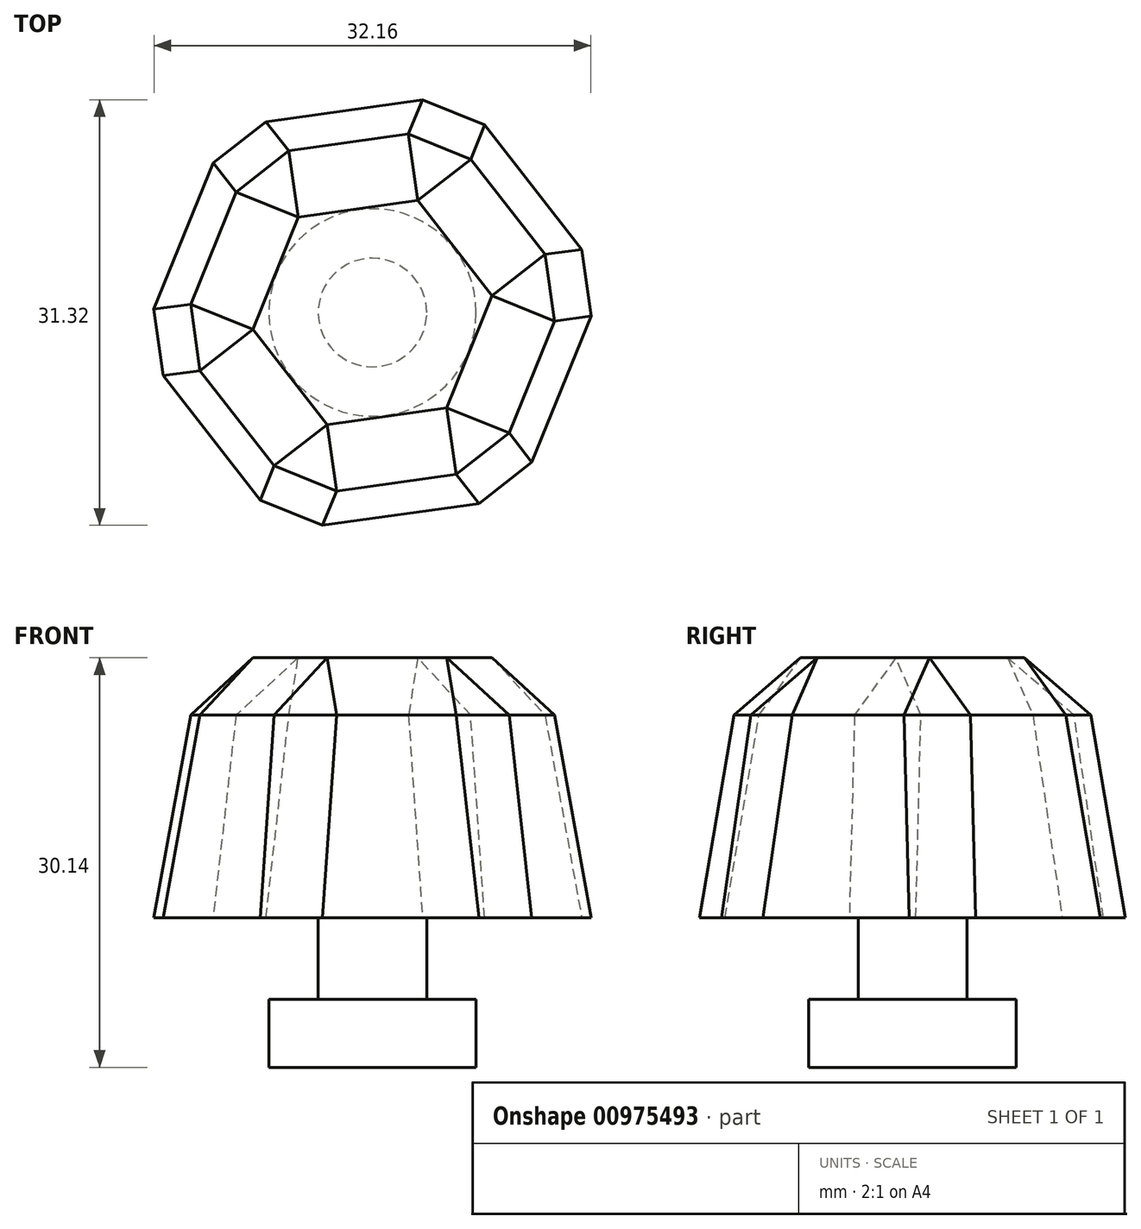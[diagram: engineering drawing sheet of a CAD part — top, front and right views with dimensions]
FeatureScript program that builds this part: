
annotation { "Feature Type Name" : "Feature", "Feature Type Description" : "" }
export const myFeature = defineFeature(function(context is Context, id is Id, definition is map)
    precondition{}
    {
        {
            var Q0;
            Q0=qCreatedBy(makeId("Top.planeOp"),FACE);
            var sketch = newSketch(context, id + "F0", { "sketchPlane" : qUnion([Q0])});
            skCircle(sketch, "E0.cCircle", {"center": v(0, 0) * mm, "radius": 15 * mm, "construction": true});
            skLineSegment(sketch, "E0.0", {"start": v(17.15, 2.4) * mm, "end": v(10.66, -13.65) * mm});
            skLineSegment(sketch, "E0.1", {"start": v(10.66, -13.65) * mm, "end": v(-6.5, -16.06) * mm});
            skLineSegment(sketch, "E0.2", {"start": v(-6.5, -16.06) * mm, "end": v(-17.15, -2.4) * mm});
            skLineSegment(sketch, "E0.3", {"start": v(-17.15, -2.4) * mm, "end": v(-10.66, 13.65) * mm});
            skLineSegment(sketch, "E0.4", {"start": v(-10.66, 13.65) * mm, "end": v(6.5, 16.06) * mm});
            skLineSegment(sketch, "E0.5", {"start": v(6.5, 16.06) * mm, "end": v(17.15, 2.4) * mm});
            skPoint(sketch, "E0.0.midPoint", {"position": v(13.9, -5.63) * mm});
            skSolve(sketch);
        }
        {
            var Q0;
            Q0=makeQuery(id+"F0.imprint","IMPRINT",FACE,{"disambiguationData":[TD([[makeQuery(id+"F0.imprint","IMPRINT",EDGE,{"derivedFrom":sQuery(id+"F0.wireOp",EDGE,"E0.0")}),-1.0]])]});
            extrude(context, id + "F1", {"entities" : qUnion([Q0]), "depth" : 19.14 * mm, "offsetDistance" : 25 * mm, "hasDraft" : true, "draftAngle" : 9 * degree, "draftPullDirection" : true});
        }
        {
            var Q0;
            Q0=makeQuery(id+"F1.opExtrude","CAP_FACE",FACE,{"disambiguationData":[OSD([sQuery(id+"F0.wireOp",EDGE,"E0.0"),sQuery(id+"F0.wireOp",EDGE,"E0.1"),sQuery(id+"F0.wireOp",EDGE,"E0.2"),sQuery(id+"F0.wireOp",EDGE,"E0.3"),sQuery(id+"F0.wireOp",EDGE,"E0.4"),sQuery(id+"F0.wireOp",EDGE,"E0.5")])],"isStart":true});
            var sketch = newSketch(context, id + "F2", { "sketchPlane" : qUnion([Q0])});
            skCircle(sketch, "E1", {"center": v(0, 0) * mm, "radius": 4 * mm});
            skSolve(sketch);
        }
        {
            var Q0;
            Q0=makeQuery(id+"F2.imprint","IMPRINT",FACE,{"disambiguationData":[TD([[makeQuery(id+"F2.imprint","IMPRINT",EDGE,{"derivedFrom":sQuery(id+"F2.wireOp",EDGE,"E1")}),1.0]])]});
            extrude(context, id + "F3", {"entities" : qUnion([Q0]), "depth" : 6 * mm, "offsetDistance" : 25 * mm});
        }
        {
            var Q0;
            Q0=makeQuery(id+"F3.opExtrude","CAP_FACE",FACE,{"disambiguationData":[OSD([sQuery(id+"F2.wireOp",EDGE,"E1")])],"isStart":false});
            var sketch = newSketch(context, id + "F4", { "sketchPlane" : qUnion([Q0])});
            skCircle(sketch, "E2", {"center": v(0, 0) * mm, "radius": 7.63 * mm});
            skSolve(sketch);
        }
        {
            var Q0;
            Q0=makeQuery(id+"F4.imprint","IMPRINT",FACE,{"disambiguationData":[TD([[makeQuery(id+"F4.imprint","IMPRINT",EDGE,{"derivedFrom":sQuery(id+"F4.wireOp",EDGE,"E2")}),1.0]])]});
            var Q1;
            Q1=makeQuery(id+"F4.imprint","IMPRINT",FACE,{"disambiguationData":[TD([[makeQuery(id+"F4.imprint","IMPRINT",EDGE,{"derivedFrom":makeQuery(id+"F3.opExtrude","CAP_EDGE",EDGE,{"disambiguationData":[OSD([sQuery(id+"F2.wireOp",EDGE,"E1")])],"isStart":false})}),1.0]])]});
            extrude(context, id + "F5", {"entities" : qUnion([Q0, Q1]), "depth" : 5 * mm, "offsetDistance" : 25 * mm});
        }
        {
            var Q0;
            Q0=makeQuery(id+"F1.opExtrude","CAP_EDGE",EDGE,{"disambiguationData":[OSD([sQuery(id+"F0.wireOp",EDGE,"E0.1")])],"isStart":false});
            var Q1;
            Q1=makeQuery(id+"F1.opExtrude","CAP_EDGE",EDGE,{"disambiguationData":[OSD([sQuery(id+"F0.wireOp",EDGE,"E0.2")])],"isStart":false});
            var Q2;
            Q2=makeQuery(id+"F1.opExtrude","CAP_EDGE",EDGE,{"disambiguationData":[OSD([sQuery(id+"F0.wireOp",EDGE,"E0.3")])],"isStart":false});
            var Q3;
            Q3=makeQuery(id+"F1.opExtrude","CAP_FACE",FACE,{"disambiguationData":[OSD([sQuery(id+"F0.wireOp",EDGE,"E0.0"),sQuery(id+"F0.wireOp",EDGE,"E0.1"),sQuery(id+"F0.wireOp",EDGE,"E0.2"),sQuery(id+"F0.wireOp",EDGE,"E0.3"),sQuery(id+"F0.wireOp",EDGE,"E0.4"),sQuery(id+"F0.wireOp",EDGE,"E0.5")])],"isStart":false});
            var Q4;
            Q4=makeQuery(id+"F1.opExtrude","SWEPT_EDGE",EDGE,{"disambiguationData":[OSD([sQuery(id+"F0.wireOp",EDGE,"E0.2"),sQuery(id+"F0.wireOp",EDGE,"E0.3")])]});
            var Q5;
            Q5=makeQuery(id+"F1.opExtrude","SWEPT_EDGE",EDGE,{"disambiguationData":[OSD([sQuery(id+"F0.wireOp",EDGE,"E0.3"),sQuery(id+"F0.wireOp",EDGE,"E0.4")])]});
            var Q6;
            Q6=makeQuery(id+"F1.opExtrude","SWEPT_EDGE",EDGE,{"disambiguationData":[OSD([sQuery(id+"F0.wireOp",EDGE,"E0.4"),sQuery(id+"F0.wireOp",EDGE,"E0.5")])]});
            var Q7;
            Q7=makeQuery(id+"F1.opExtrude","SWEPT_EDGE",EDGE,{"disambiguationData":[OSD([sQuery(id+"F0.wireOp",EDGE,"E0.0"),sQuery(id+"F0.wireOp",EDGE,"E0.5")])]});
            var Q8;
            Q8=makeQuery(id+"F1.opExtrude","SWEPT_EDGE",EDGE,{"disambiguationData":[OSD([sQuery(id+"F0.wireOp",EDGE,"E0.1"),sQuery(id+"F0.wireOp",EDGE,"E0.2")])]});
            var Q9;
            Q9=makeQuery(id+"F1.opExtrude","SWEPT_EDGE",EDGE,{"disambiguationData":[OSD([sQuery(id+"F0.wireOp",EDGE,"E0.0"),sQuery(id+"F0.wireOp",EDGE,"E0.1")])]});
            chamfer(context, id + "F6", {"entities" : qUnion([Q0, Q1, Q2, Q3, Q4, Q5, Q6, Q7, Q8, Q9]), "width" : 5 * mm, "tangentPropagation" : true});
        }
    });
